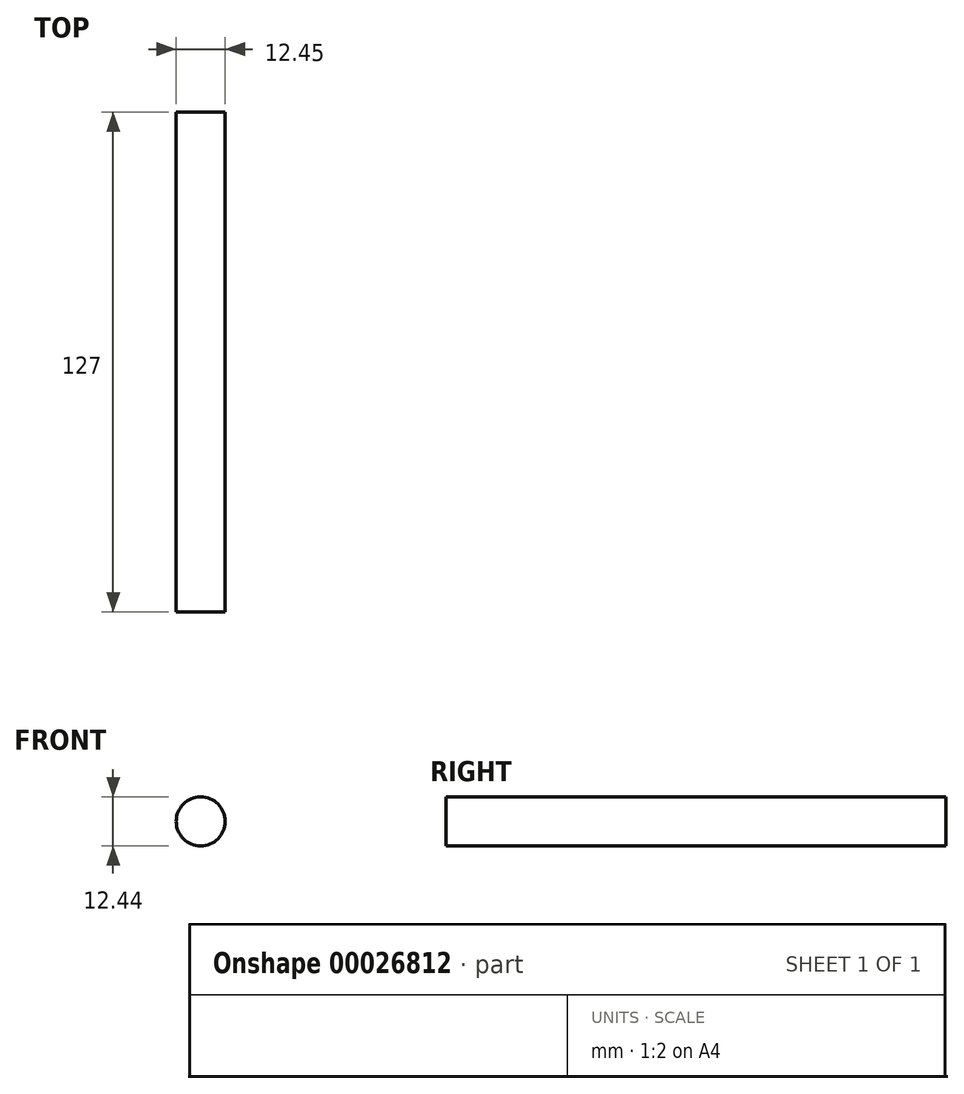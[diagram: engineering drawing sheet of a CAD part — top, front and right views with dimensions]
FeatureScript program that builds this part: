
annotation { "Feature Type Name" : "Feature", "Feature Type Description" : "" }
export const myFeature = defineFeature(function(context is Context, id is Id, definition is map)
    precondition{}
    {
        {
            var Q0;
            Q0=qCreatedBy(makeId("Front.planeOp"),FACE);
            var sketch = newSketch(context, id + "F0", { "sketchPlane" : qUnion([Q0])});
            skCircle(sketch, "E0", {"center": v(-14.3, -4.62) * mm, "radius": 6.22 * mm});
            skSolve(sketch);
        }
        {
            var Q0;
            Q0=makeQuery(id+"F0.imprint","IMPRINT",FACE,{"disambiguationData":[TD([[makeQuery(id+"F0.imprint","IMPRINT",EDGE,{"derivedFrom":sQuery(id+"F0.wireOp",EDGE,"E0")}),1.0]])]});
            extrude(context, id + "F1", {"entities" : qUnion([Q0]), "depth" : 127 * mm});
        }
    });
